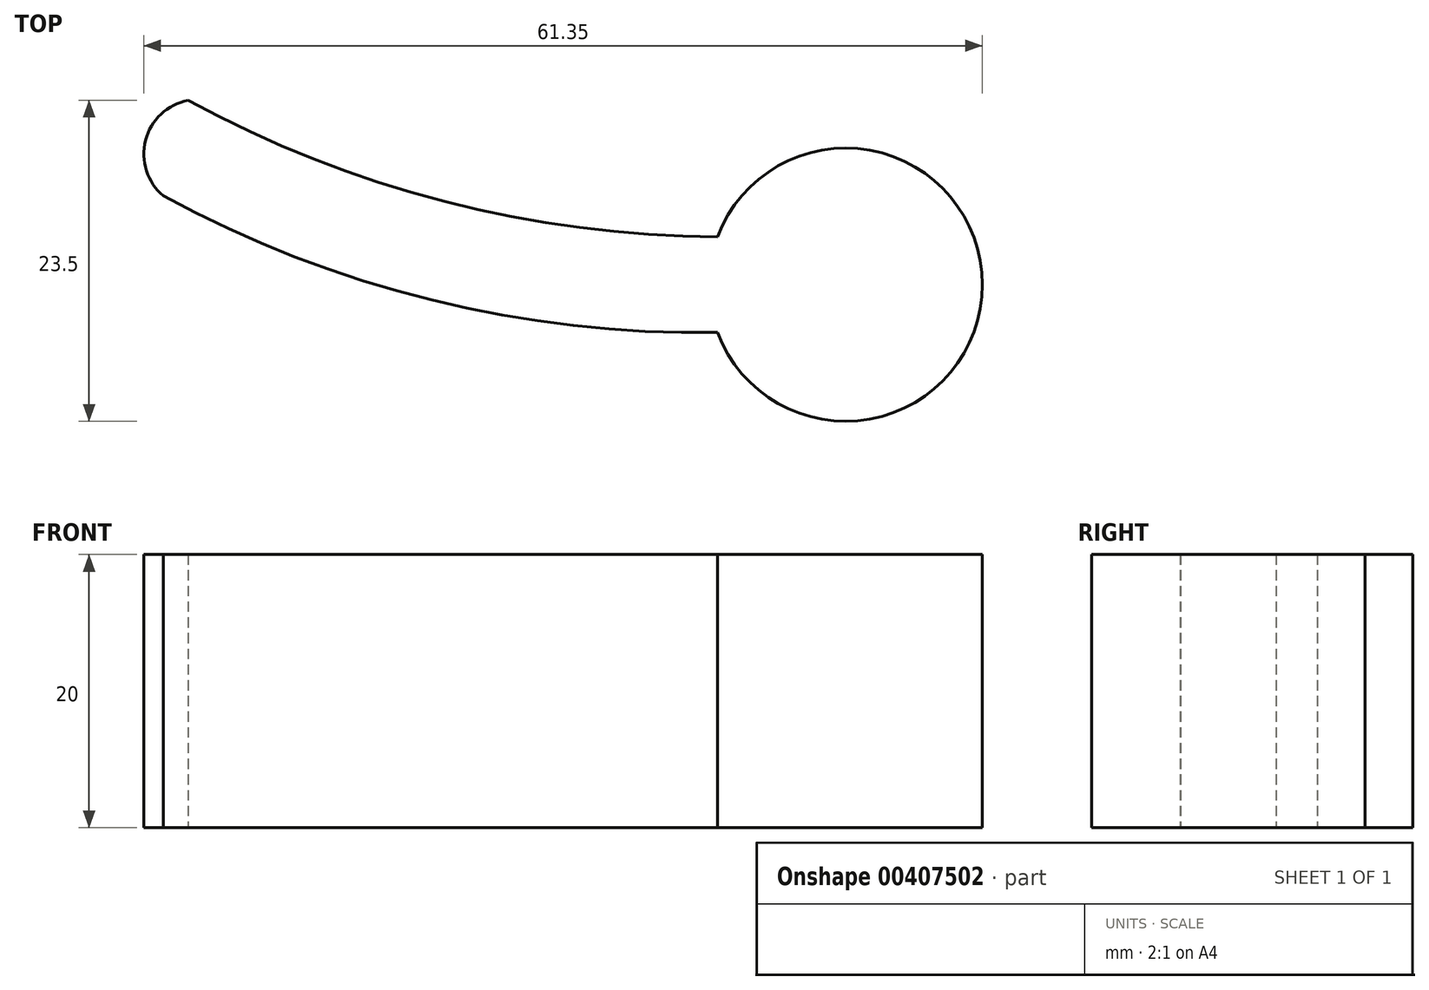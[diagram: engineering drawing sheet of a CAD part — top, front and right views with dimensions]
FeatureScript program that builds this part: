
annotation { "Feature Type Name" : "Feature", "Feature Type Description" : "" }
export const myFeature = defineFeature(function(context is Context, id is Id, definition is map)
    precondition{}
    {
        {
            var Q0;
            Q0=qCreatedBy(makeId("Top.planeOp"),FACE);
            var sketch = newSketch(context, id + "F0", { "sketchPlane" : qUnion([Q0])});
            skLineSegment(sketch, "E0", {"start": v(0, 0) * mm, "end": v(-38.73, 10) * mm, "construction": true});
            skLineSegment(sketch, "E1", {"start": v(0, 0) * mm, "end": v(-38.73, 0) * mm, "construction": true});
            skArc(sketch, "E2", {"start": v(-38.73, 10) * mm, "mid": v(-19.98, 2.6) * mm, "end": v(0, 0) * mm});
            skLineSegment(sketch, "E3", {"start": v(0, 0) * mm, "end": v(0, -7) * mm, "construction": true});
            skArc(sketch, "E4", {"start": v(-40.54, 3) * mm, "mid": v(-20.92, -4.62) * mm, "end": v(0, -7) * mm});
            skArc(sketch, "E5", {"start": v(0, -7) * mm, "mid": v(19.37, -3.5) * mm, "end": v(0, 0) * mm});
            skLineSegment(sketch, "E6", {"start": v(-38.73, 10) * mm, "end": v(-40.93, 1.48) * mm, "construction": true});
            skArc(sketch, "E7", {"start": v(-38.73, 10) * mm, "mid": v(-41.85, 7.07) * mm, "end": v(-40.54, 3) * mm});
            skSolve(sketch);
        }
        {
            var Q0;
            Q0=makeQuery(id+"F0.imprint","IMPRINT",FACE,{"disambiguationData":[TD([[makeQuery(id+"F0.imprint","IMPRINT",EDGE,{"derivedFrom":sQuery(id+"F0.wireOp",EDGE,"E2")}),-1.0]])]});
            extrude(context, id + "F1", {"entities" : qUnion([Q0]), "depth" : 20 * mm});
        }
    });
